# Revit family: kawneer-flushline_novl-pr_tran-fr_20644
name_source: partatom
category: Doors
revit_build: Autodesk Revit 2015 (Build: 20140905_0730(x64)
units: mm (PartAtom-declared; Revit-internal decimal feet)

## types (1)
- kawneer-flushline_novl-pr_tran-fr_20644
    2-Color Option = no
    Air Infiltration (ASTM E 283) = product not tested
    Application = moderate traffic, high traffic, impact areas
    Assembly Code = B2030110
    CSI Masterformat Code = 08 41 13
    Color = any
    Depth = 2"
    Description = The "Flushline" entrance is a polyurethane foam filled door with FRP or aluminum face sheets designed in various textures for interior or exterior use.
    Door Corner Construction = Welded
    Door Opening = 60 1/2"
    Door Panel Height = 84"
    Door Panel Material = Aluminum - ASTM B 221 - 6063-T6 alloy and temper
    Door Panel Width = 30 1/4"
    Function = Interior
    Function (Interior or Exterior) = Exterior, Interior
    Glass Capture = Captured
    Glass Installtion = cut outs for vision area, inside or outside
    Glass U-Factor = product not tested
    Glazing Thickness = 0"
    Height = 96"
    Hinging Types = Offset Pivot, Butt Hinge, Continuous Gear Hinge
    Keywords = Entrance, Door, Swing Door, FRP Skin Door, Aluminum Skin Door, Foam-filled Door
    Manufacturer = Kawneer
    Manufacturer Part Number = Flushline®
    Model = Flushline®
    Overall U-Factor = product not tested
    Panel Inserts Material = Glass
    Product data url = https://bimobject.com
    Short Description = Foam-filled with Aluminum or FRP Face Sheets
    Sightline = 0"
    Thermal Transmittance = < 0.28 BTU/hr/sf/F
    Type Comments = Foam-filled with Aluminum or FRP Face Sheets
    Type of Glazing = monolithic, insulating
    URL = http://www.kawneer.com
    Wall Closure = By host
    Water - Static (ASTM E 331) = product not tested
    Width = 64"

## geometry (parser evidence)
native form markers: Sweep x12
no freeform markers — native parametric forms only
